# Revit family: IS_iLifeA_T4524_BIM_NL
name_source: partatom
category: Plumbing Fixtures
units: mm (PartAtom-declared; Revit-internal decimal feet)

## family parameters
Always vertical = No
Cut with Voids When Loaded = No
OmniClass Number = 23.45.05.14.27
OmniClass Title = Bidets
Part Type = Normal
Room Calculation Point = No
Round Connector Dimension = Use Diameter
Shared = No
Work Plane-Based = No

## types (2) — shared parameters
Accesoires = https://www.idealstandard.nl
Accessories = https://www.idealstandard.nl
Afmetingen = 540 x 305 x 355mm
AfstandsEenheid = millimeter
AreaMeasurement = internal
AreaUnits = Millimeter
Artikelreferentie = I.life Eine wandhängende Bidet-Taschenbefestigung
Auteur = Ideal Standard
BIMObjectName = IS_IdealStandard_Bidets_I.life_T4524
BIMobject category = Bidets
BIMobject category code = sanitary-bidets
BIMobject main category = Sanitary
BIMobject main category code = sanitary
Beschrijvinggarantie = Herstellergarantie
BidetMounting = Wall_Hung
BimObjectNaam = IS_IdealStandard_Bidets_I.life_T4524
Brand = Ideal Standard
Brand url = http://https:
ConnectionType = Plumbing
CurrencyUnit = €
CurrentRevision = 1
Date of publishing = 28/06/2021
DurationUnit = Years
DuurEenheid = Jaar
Edition number = 1
Eigenschappen = Wandhängende Bidet-Taschenbefestigung
Features = Wall-Hung bidet pcket fixation
Garantieonderdelen = 5
Garantieunits = Jaar
GemaaktOp = 40722
Help = https://www.idealstandard.nl
Hoogte = 302.50276184082
Hulp = https://www.idealstandard.nl
IFC Classification = Sanitary Terminal
IfcExportAs = IfcSanitaryTerminalType
IfcExportType = BIDET
Installatieinstructies = https://www.idealstandard.nl
Installation instructions = https://www.idealstandard.nl
InstallationInstructions = https://www.idealstandard.nl
Lengte = 540 mm
LinearUnits = millimeter
MaintenanceInformation = https://www.idealstandard.nl
Manufacturer = Ideal Standard
Manufacturer name = Ideal Standard
ManufacturerURL = https://www.idealstandard.nl
Masterformat 2014 Code = 22 41 13.19
Masterformat 2014 Description = Residential Bidets
Materiaal = Vitrous China
Material = Vitrous China
Material main = Vitrous China
Merk = Ideal Standard
ModelReference = I.life A wallhung bidet pcket fixation
Montageinstuctie = https://www.idealstandard.nl
NBS Reference Code = 35-06-11
NBS Reference Description = Bidets
Name = Bidets_I.life_T4524_IdealStandard
NettWeight = 18
Nettogewicht = 18
NominalDepth = 540 mm
NominalHeight = 303 mm
NominalWidth = 354 mm
Normen = Bidets_I.life_T4524_IdealStandard
OmniClass Code = 23-31 23 00
OmniClass Description = Bidets
OppervlakteEenheid = Millimeter
Product Guid = 70050309-87bd-44e5-9a9c-cc9b021aad95
Product SKU = T4524
Product certification = https://www.idealstandard.nl
Product data url = https://bimobject.com
Product family = I.life
Product group = Bidet
Product name = I.life A wallhung bidet pcket fixation
Product url = https://www.idealstandard.nl
ProductInformation = https://www.idealstandard.nl
ProductSoort = Bidets
Productinformatie = https://www.idealstandard.nl
QR code = http://bimobject.com
Referentie = I.life Eine wandhängende Bidet-Taschenbefestigung
Revisie = 1
Shape = sculpture
Size = 540 x 305 x 355mm
Space = Internal
SpareParts = https://www.idealstandard.nl
Technical description = https://www.idealstandard.nl
Telefoonnummer = 077 355 08 08
Typeconnectie = Installation
UNSPSC Code = 30181502
URL = https://https:
Uniclass 1.4 Code = L7215
Uniclass 1.4 Description = Bidets
Uniclass 2.0 Code = PR-35-06-11
Uniclass 2.0 Description = Bidets
Uniclass 2015 Code = Pr_40_20_06_11
Uniclass 2015 Name = Bidets
Uniclass2015Beschrijving = Bidets
Uniclass2015Code = Pr_40_20_06_11
Uniclass2015Referentie = Pr_40_20_06_11
Uniclass2015Title = Bidets
Uniclass2015Version = v1.20
Urlproducent = https://https:
ValutaEenheid = €
Versie = 1
Version = 1
VolumeUnits = Liter
Volumeunits = Liter
Vorm = beeldhouwwerk
WRASURL = https://www.wrasapprovals.co.uk
WarrantyDescription = manufacturer warranty
WarrantyDurationParts = 99
WarrantyDurationUnit = years
Wisselstukken = https://www.idealstandard.nl
Youtube clip = https://www.youtube.com
zero-valued in all types: Breedte, BrutoGewicht, Cost, Diepte, DrainSize, GrootteAfvoergat, Overloop, Vervangingskosten

## per-type parameters (varying)
| type | Afwerking | Artikelnummer | Artikelomschrijving | BarCode | Barcode | Color | Description | Finish | GTIN code | Kleur | MainColor | Model | ModelNumber |
| T4524MA - I.life A wallhung bidet pcket fixation - Ideal Plus White | IdealPlusWeiß | T4524MA | I.life A wandhängende Bidet-Taschenbefestigung - Ideal Plus White | 8014140486763 | 8014140486763 | IdealPlusWeiß | I.life A wandhängende Bidet-Taschenbefestigung - Ideal Plus White | IdealPlusWeiß | https://8014140486763 | IdealPlusWeiß | IdealPlusWhite | T4524MA | T4524MA |
| T452401 - I.life A wallhung bidet pcket fixation - White | Weiß | T452401 | I.life A wandhängende Bidet-Taschenbefestigung - Weiß | 8014140485919 | 8014140485919 | Weiß | I.life A wandhängende Bidet-Taschenbefestigung - Weiß | Weiß | https://8014140485919 | Weiß | White | T452401 | T452401 |

## geometry (parser evidence)
native form markers: Sweep x2
no freeform markers — native parametric forms only
